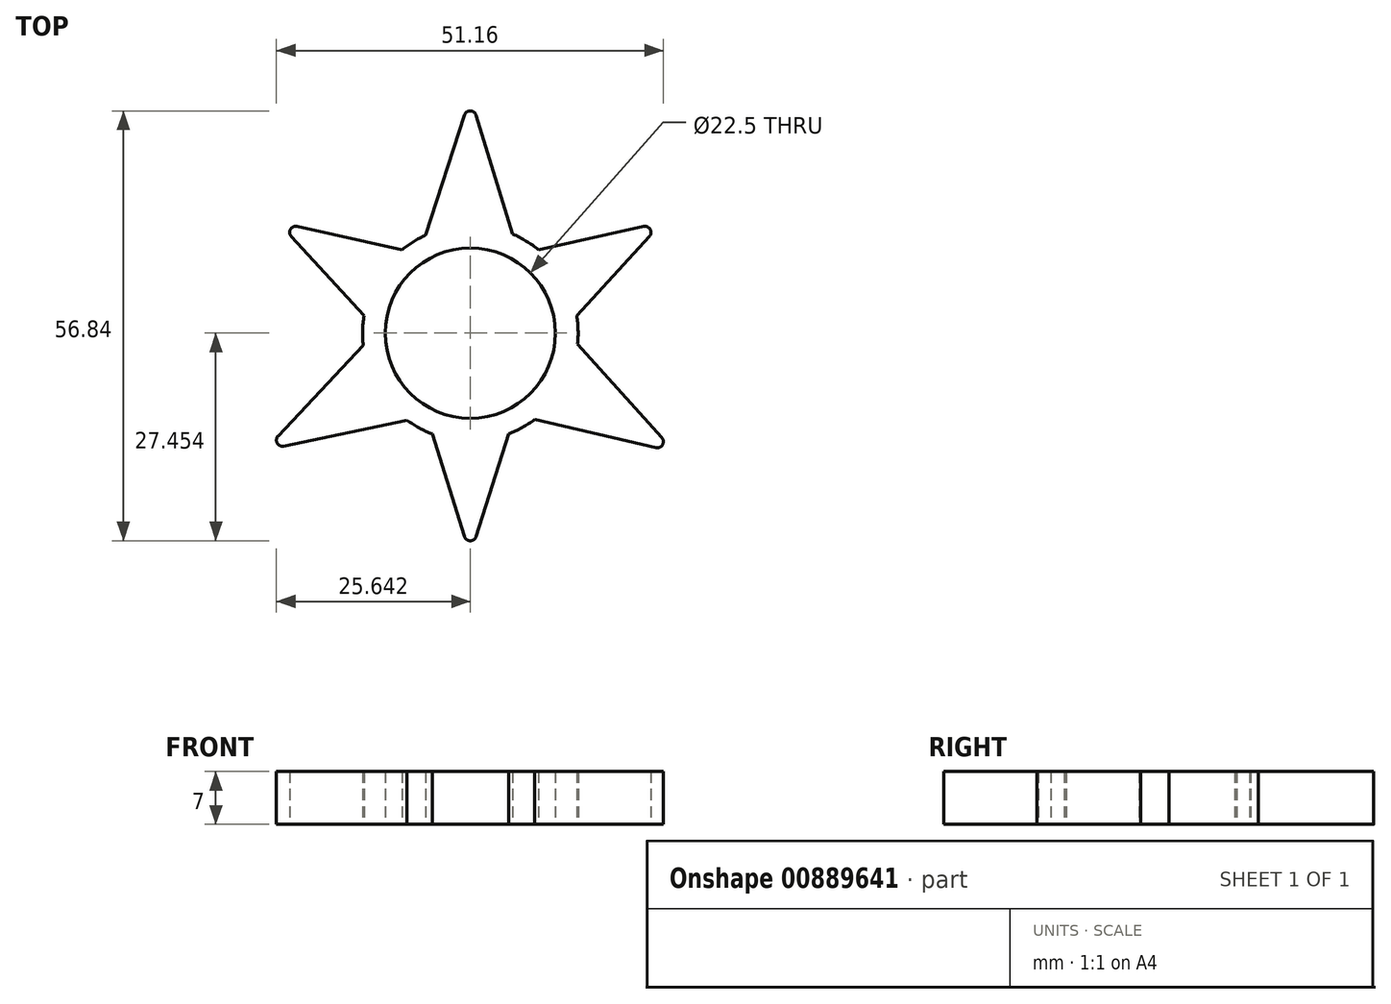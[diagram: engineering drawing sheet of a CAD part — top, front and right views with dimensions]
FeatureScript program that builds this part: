
annotation { "Feature Type Name" : "Feature", "Feature Type Description" : "" }
export const myFeature = defineFeature(function(context is Context, id is Id, definition is map)
    precondition{}
    {
        {
            var Q0;
            Q0=qCreatedBy(makeId("Top.planeOp"),FACE);
            var sketch = newSketch(context, id + "F0", { "sketchPlane" : qUnion([Q0])});
            skCircle(sketch, "E0", {"center": v(-0.33, -1.96) * mm, "radius": 11.25 * mm});
            skLineSegment(sketch, "E1", {"start": v(-7.64, 6.6) * mm, "end": v(-0.33, 29.3) * mm});
            skLineSegment(sketch, "E2", {"start": v(-0.33, 29.3) * mm, "end": v(6.57, 6.93) * mm});
            skLineSegment(sketch, "E3.1.0", {"start": v(26.68, -17.67) * mm, "end": v(3.88, -12.39) * mm});
            skLineSegment(sketch, "E3.1.1", {"start": v(10.74, 0.06) * mm, "end": v(26.68, -17.67) * mm});
            skLineSegment(sketch, "E3.2.0", {"start": v(-27.5, -17.4) * mm, "end": v(-11.46, -0.35) * mm});
            skLineSegment(sketch, "E3.2.1", {"start": v(-4.15, -12.54) * mm, "end": v(-27.5, -17.4) * mm});
            skLineSegment(sketch, "E4", {"start": v(-6.63, -11.27) * mm, "end": v(-0.33, -31.27) * mm});
            skLineSegment(sketch, "E5", {"start": v(-0.33, -31.27) * mm, "end": v(5.98, -11.27) * mm});
            skLineSegment(sketch, "E6.1.0", {"start": v(25.06, 12.7) * mm, "end": v(4.59, 8.16) * mm});
            skLineSegment(sketch, "E6.1.1", {"start": v(10.9, -2.76) * mm, "end": v(25.06, 12.7) * mm});
            skLineSegment(sketch, "E6.2.0", {"start": v(-25.72, 12.7) * mm, "end": v(-11.55, -2.76) * mm});
            skLineSegment(sketch, "E6.2.1", {"start": v(-5.24, 8.16) * mm, "end": v(-25.72, 12.7) * mm});
            skCircle(sketch, "E7", {"center": v(-0.33, -1.96) * mm, "radius": 14.25 * mm});
            skSolve(sketch);
        }
        {
            var Q0;
            {var subQ1=sQuery(id+"F0.wireOp",EDGE,"E0");var subQ5=sQuery(id+"F0.wireOp",EDGE,"E1");var subQ6=makeQuery(id+"F0.imprint","INTERSECT",VERTEX,{"derivedFrom":[subQ1,subQ5]});Q0=makeQuery(id+"F0.imprint","IMPRINT",FACE,{"disambiguationData":[TD([[makeQuery(id+"F0.imprint","IMPRINT",EDGE,{"disambiguationData":[TD([[subQ6,-1.0]])],"derivedFrom":subQ1}),-1.0]])]});}
            var Q1;
            {var subQ0=sQuery(id+"F0.wireOp",EDGE,"E7");var subQ1=sQuery(id+"F0.wireOp",EDGE,"E1");var subQ2=makeQuery(id+"F0.imprint","INTERSECT",VERTEX,{"derivedFrom":[subQ1,subQ0]});Q1=makeQuery(id+"F0.imprint","IMPRINT",FACE,{"disambiguationData":[TD([[makeQuery(id+"F0.imprint","IMPRINT",EDGE,{"disambiguationData":[TD([[subQ2,1.0]])],"derivedFrom":subQ1}),1.0]])]});}
            var Q2;
            {var subQ1=sQuery(id+"F0.wireOp",EDGE,"E0");var subQ5=sQuery(id+"F0.wireOp",EDGE,"E2");var subQ6=makeQuery(id+"F0.imprint","INTERSECT",VERTEX,{"derivedFrom":[subQ1,subQ5]});Q2=makeQuery(id+"F0.imprint","IMPRINT",FACE,{"disambiguationData":[TD([[makeQuery(id+"F0.imprint","IMPRINT",EDGE,{"disambiguationData":[TD([[subQ6,-1.0]])],"derivedFrom":subQ1}),-1.0]])]});}
            var Q3;
            {var subQ0=sQuery(id+"F0.wireOp",EDGE,"E2");var subQ1=sQuery(id+"F0.wireOp",EDGE,"E0");var subQ2=makeQuery(id+"F0.imprint","INTERSECT",VERTEX,{"derivedFrom":[subQ1,subQ0]});Q3=makeQuery(id+"F0.imprint","IMPRINT",FACE,{"disambiguationData":[TD([[makeQuery(id+"F0.imprint","IMPRINT",EDGE,{"disambiguationData":[TD([[subQ2,1.0]])],"derivedFrom":subQ1}),-1.0]])]});}
            var Q4;
            {var subQ3=sQuery(id+"F0.wireOp",EDGE,"E3.1.1");var subQ6=sQuery(id+"F0.wireOp",EDGE,"E0");var subQ9=makeQuery(id+"F0.imprint","INTERSECT",VERTEX,{"derivedFrom":[subQ6,subQ3]});Q4=makeQuery(id+"F0.imprint","IMPRINT",FACE,{"disambiguationData":[TD([[makeQuery(id+"F0.imprint","IMPRINT",EDGE,{"disambiguationData":[TD([[subQ9,-1.0]])],"derivedFrom":subQ6}),-1.0]])]});}
            var Q5;
            {var subQ1=sQuery(id+"F0.wireOp",EDGE,"E0");var subQ7=sQuery(id+"F0.wireOp",EDGE,"E3.1.0");var subQ8=makeQuery(id+"F0.imprint","INTERSECT",VERTEX,{"derivedFrom":[subQ1,subQ7]});Q5=makeQuery(id+"F0.imprint","IMPRINT",FACE,{"disambiguationData":[TD([[makeQuery(id+"F0.imprint","IMPRINT",EDGE,{"disambiguationData":[TD([[subQ8,-1.0]])],"derivedFrom":subQ1}),-1.0]])]});}
            var Q6;
            {var subQ0=sQuery(id+"F0.wireOp",EDGE,"E3.1.0");var subQ1=sQuery(id+"F0.wireOp",EDGE,"E0");var subQ2=makeQuery(id+"F0.imprint","INTERSECT",VERTEX,{"derivedFrom":[subQ1,subQ0]});Q6=makeQuery(id+"F0.imprint","IMPRINT",FACE,{"disambiguationData":[TD([[makeQuery(id+"F0.imprint","IMPRINT",EDGE,{"disambiguationData":[TD([[subQ2,1.0]])],"derivedFrom":subQ1}),-1.0]])]});}
            var Q7;
            {var subQ1=sQuery(id+"F0.wireOp",EDGE,"E0");var subQ5=sQuery(id+"F0.wireOp",EDGE,"E3.2.1");var subQ6=makeQuery(id+"F0.imprint","INTERSECT",VERTEX,{"derivedFrom":[subQ1,subQ5]});Q7=makeQuery(id+"F0.imprint","IMPRINT",FACE,{"disambiguationData":[TD([[makeQuery(id+"F0.imprint","IMPRINT",EDGE,{"disambiguationData":[TD([[subQ6,-1.0]])],"derivedFrom":subQ1}),-1.0]])]});}
            var Q8;
            {var subQ5=sQuery(id+"F0.wireOp",EDGE,"E3.2.0");var subQ6=sQuery(id+"F0.wireOp",EDGE,"E0");var subQ7=makeQuery(id+"F0.imprint","INTERSECT",VERTEX,{"derivedFrom":[subQ6,subQ5]});Q8=makeQuery(id+"F0.imprint","IMPRINT",FACE,{"disambiguationData":[TD([[makeQuery(id+"F0.imprint","IMPRINT",EDGE,{"disambiguationData":[TD([[subQ7,-1.0]])],"derivedFrom":subQ6}),-1.0]])]});}
            var Q9;
            {var subQ0=sQuery(id+"F0.wireOp",EDGE,"E6.2.1");var subQ1=sQuery(id+"F0.wireOp",EDGE,"E6.2.0");var subQ2=makeQuery(id+"F0.imprint","INTERSECT",VERTEX,{"derivedFrom":[subQ1,subQ0]});Q9=makeQuery(id+"F0.imprint","IMPRINT",FACE,{"disambiguationData":[TD([[makeQuery(id+"F0.imprint","IMPRINT",EDGE,{"disambiguationData":[TD([[subQ2,-1.0]])],"derivedFrom":subQ1}),1.0]])]});}
            var Q10;
            {var subQ0=sQuery(id+"F0.wireOp",EDGE,"E2");var subQ1=sQuery(id+"F0.wireOp",EDGE,"E1");var subQ2=makeQuery(id+"F0.imprint","INTERSECT",VERTEX,{"derivedFrom":[subQ1,subQ0]});Q10=makeQuery(id+"F0.imprint","IMPRINT",FACE,{"disambiguationData":[TD([[makeQuery(id+"F0.imprint","IMPRINT",EDGE,{"disambiguationData":[TD([[subQ2,1.0]])],"derivedFrom":subQ1}),-1.0]])]});}
            var Q11;
            {var subQ0=sQuery(id+"F0.wireOp",EDGE,"E6.1.1");var subQ1=sQuery(id+"F0.wireOp",EDGE,"E6.1.0");var subQ2=makeQuery(id+"F0.imprint","INTERSECT",VERTEX,{"derivedFrom":[subQ1,subQ0]});Q11=makeQuery(id+"F0.imprint","IMPRINT",FACE,{"disambiguationData":[TD([[makeQuery(id+"F0.imprint","IMPRINT",EDGE,{"disambiguationData":[TD([[subQ2,-1.0]])],"derivedFrom":subQ1}),1.0]])]});}
            var Q12;
            {var subQ0=sQuery(id+"F0.wireOp",EDGE,"E3.1.1");var subQ1=sQuery(id+"F0.wireOp",EDGE,"E3.1.0");var subQ2=makeQuery(id+"F0.imprint","INTERSECT",VERTEX,{"derivedFrom":[subQ1,subQ0]});Q12=makeQuery(id+"F0.imprint","IMPRINT",FACE,{"disambiguationData":[TD([[makeQuery(id+"F0.imprint","IMPRINT",EDGE,{"disambiguationData":[TD([[subQ2,-1.0]])],"derivedFrom":subQ1}),-1.0]])]});}
            var Q13;
            {var subQ0=sQuery(id+"F0.wireOp",EDGE,"E5");var subQ1=sQuery(id+"F0.wireOp",EDGE,"E4");var subQ2=makeQuery(id+"F0.imprint","INTERSECT",VERTEX,{"derivedFrom":[subQ1,subQ0]});Q13=makeQuery(id+"F0.imprint","IMPRINT",FACE,{"disambiguationData":[TD([[makeQuery(id+"F0.imprint","IMPRINT",EDGE,{"disambiguationData":[TD([[subQ2,1.0]])],"derivedFrom":subQ1}),1.0]])]});}
            var Q14;
            {var subQ0=sQuery(id+"F0.wireOp",EDGE,"E3.2.1");var subQ1=sQuery(id+"F0.wireOp",EDGE,"E3.2.0");var subQ2=makeQuery(id+"F0.imprint","INTERSECT",VERTEX,{"derivedFrom":[subQ1,subQ0]});Q14=makeQuery(id+"F0.imprint","IMPRINT",FACE,{"disambiguationData":[TD([[makeQuery(id+"F0.imprint","IMPRINT",EDGE,{"disambiguationData":[TD([[subQ2,-1.0]])],"derivedFrom":subQ1}),-1.0]])]});}
            var Q15;
            {var subQ0=sQuery(id+"F0.wireOp",EDGE,"E3.2.0");var subQ1=sQuery(id+"F0.wireOp",EDGE,"E0");var subQ2=makeQuery(id+"F0.imprint","INTERSECT",VERTEX,{"derivedFrom":[subQ1,subQ0]});Q15=makeQuery(id+"F0.imprint","IMPRINT",FACE,{"disambiguationData":[TD([[makeQuery(id+"F0.imprint","IMPRINT",EDGE,{"disambiguationData":[TD([[subQ2,1.0]])],"derivedFrom":subQ1}),-1.0]])]});}
            var Q16;
            {var subQ0=sQuery(id+"F0.wireOp",EDGE,"E7");var subQ1=sQuery(id+"F0.wireOp",EDGE,"E3.2.1");var subQ2=makeQuery(id+"F0.imprint","INTERSECT",VERTEX,{"derivedFrom":[subQ1,subQ0]});Q16=makeQuery(id+"F0.imprint","IMPRINT",FACE,{"disambiguationData":[TD([[makeQuery(id+"F0.imprint","IMPRINT",EDGE,{"disambiguationData":[TD([[subQ2,1.0]])],"derivedFrom":subQ1}),1.0]])]});}
            var Q17;
            {var subQ0=sQuery(id+"F0.wireOp",EDGE,"E7");var subQ1=sQuery(id+"F0.wireOp",EDGE,"E3.1.1");var subQ2=makeQuery(id+"F0.imprint","INTERSECT",VERTEX,{"derivedFrom":[subQ1,subQ0]});Q17=makeQuery(id+"F0.imprint","IMPRINT",FACE,{"disambiguationData":[TD([[makeQuery(id+"F0.imprint","IMPRINT",EDGE,{"disambiguationData":[TD([[subQ2,1.0]])],"derivedFrom":subQ1}),1.0]])]});}
            var Q18;
            {var subQ0=sQuery(id+"F0.wireOp",EDGE,"E7");var subQ1=sQuery(id+"F0.wireOp",EDGE,"E3.2.0");var subQ2=makeQuery(id+"F0.imprint","INTERSECT",VERTEX,{"derivedFrom":[subQ1,subQ0]});Q18=makeQuery(id+"F0.imprint","IMPRINT",FACE,{"disambiguationData":[TD([[makeQuery(id+"F0.imprint","IMPRINT",EDGE,{"disambiguationData":[TD([[subQ2,-1.0]])],"derivedFrom":subQ1}),1.0]])]});}
            var Q19;
            {var subQ3=sQuery(id+"F0.wireOp",EDGE,"E4");var subQ5=sQuery(id+"F0.wireOp",EDGE,"E0");var subQ6=makeQuery(id+"F0.imprint","INTERSECT",VERTEX,{"derivedFrom":[subQ5,subQ3]});Q19=makeQuery(id+"F0.imprint","IMPRINT",FACE,{"disambiguationData":[TD([[makeQuery(id+"F0.imprint","IMPRINT",EDGE,{"disambiguationData":[TD([[subQ6,1.0]])],"derivedFrom":subQ5}),-1.0]])]});}
            var Q20;
            {var subQ0=sQuery(id+"F0.wireOp",EDGE,"E3.2.1");var subQ1=sQuery(id+"F0.wireOp",EDGE,"E0");var subQ2=makeQuery(id+"F0.imprint","INTERSECT",VERTEX,{"derivedFrom":[subQ1,subQ0]});Q20=makeQuery(id+"F0.imprint","IMPRINT",FACE,{"disambiguationData":[TD([[makeQuery(id+"F0.imprint","IMPRINT",EDGE,{"disambiguationData":[TD([[subQ2,1.0]])],"derivedFrom":subQ1}),-1.0]])]});}
            var Q21;
            {var subQ0=sQuery(id+"F0.wireOp",EDGE,"E7");var subQ1=sQuery(id+"F0.wireOp",EDGE,"E3.1.0");var subQ2=makeQuery(id+"F0.imprint","INTERSECT",VERTEX,{"derivedFrom":[subQ1,subQ0]});Q21=makeQuery(id+"F0.imprint","IMPRINT",FACE,{"disambiguationData":[TD([[makeQuery(id+"F0.imprint","IMPRINT",EDGE,{"disambiguationData":[TD([[subQ2,-1.0]])],"derivedFrom":subQ1}),1.0]])]});}
            var Q22;
            {var subQ7=sQuery(id+"F0.wireOp",EDGE,"E5");var subQ9=sQuery(id+"F0.wireOp",EDGE,"E0");var subQ10=makeQuery(id+"F0.imprint","INTERSECT",VERTEX,{"derivedFrom":[subQ9,subQ7]});Q22=makeQuery(id+"F0.imprint","IMPRINT",FACE,{"disambiguationData":[TD([[makeQuery(id+"F0.imprint","IMPRINT",EDGE,{"disambiguationData":[TD([[subQ10,-1.0]])],"derivedFrom":subQ9}),-1.0]])]});}
            var Q23;
            {var subQ0=sQuery(id+"F0.wireOp",EDGE,"E3.1.1");var subQ1=sQuery(id+"F0.wireOp",EDGE,"E0");var subQ2=makeQuery(id+"F0.imprint","INTERSECT",VERTEX,{"derivedFrom":[subQ1,subQ0]});Q23=makeQuery(id+"F0.imprint","IMPRINT",FACE,{"disambiguationData":[TD([[makeQuery(id+"F0.imprint","IMPRINT",EDGE,{"disambiguationData":[TD([[subQ2,1.0]])],"derivedFrom":subQ1}),-1.0]])]});}
            var Q24;
            {var subQ3=sQuery(id+"F0.wireOp",EDGE,"E6.1.0");var subQ5=sQuery(id+"F0.wireOp",EDGE,"E0");var subQ6=makeQuery(id+"F0.imprint","INTERSECT",VERTEX,{"derivedFrom":[subQ5,subQ3]});Q24=makeQuery(id+"F0.imprint","IMPRINT",FACE,{"disambiguationData":[TD([[makeQuery(id+"F0.imprint","IMPRINT",EDGE,{"disambiguationData":[TD([[subQ6,-1.0]])],"derivedFrom":subQ5}),-1.0]])]});}
            var Q25;
            {var subQ0=sQuery(id+"F0.wireOp",EDGE,"E7");var subQ1=sQuery(id+"F0.wireOp",EDGE,"E2");var subQ2=makeQuery(id+"F0.imprint","INTERSECT",VERTEX,{"derivedFrom":[subQ1,subQ0]});Q25=makeQuery(id+"F0.imprint","IMPRINT",FACE,{"disambiguationData":[TD([[makeQuery(id+"F0.imprint","IMPRINT",EDGE,{"disambiguationData":[TD([[subQ2,-1.0]])],"derivedFrom":subQ1}),1.0]])]});}
            var Q26;
            {var subQ0=sQuery(id+"F0.wireOp",EDGE,"E1");var subQ1=sQuery(id+"F0.wireOp",EDGE,"E0");var subQ2=makeQuery(id+"F0.imprint","INTERSECT",VERTEX,{"derivedFrom":[subQ1,subQ0]});Q26=makeQuery(id+"F0.imprint","IMPRINT",FACE,{"disambiguationData":[TD([[makeQuery(id+"F0.imprint","IMPRINT",EDGE,{"disambiguationData":[TD([[subQ2,1.0]])],"derivedFrom":subQ1}),-1.0]])]});}
            extrude(context, id + "F1", {"entities" : qUnion([Q0, Q1, Q2, Q3, Q4, Q5, Q6, Q7, Q8, Q9, Q10, Q11, Q12, Q13, Q14, Q15, Q16, Q17, Q18, Q19, Q20, Q21, Q22, Q23, Q24, Q25, Q26]), "depth" : 7 * mm, "offsetDistance" : 25 * mm});
        }
        {
            var Q0;
            Q0=makeQuery(id+"F1.opExtrude","SWEPT_EDGE",EDGE,{"disambiguationData":[OSD([sQuery(id+"F0.wireOp",EDGE,"E4"),sQuery(id+"F0.wireOp",EDGE,"E5")])]});
            var Q1;
            Q1=makeQuery(id+"F1.opExtrude","SWEPT_EDGE",EDGE,{"disambiguationData":[OSD([sQuery(id+"F0.wireOp",EDGE,"E3.1.0"),sQuery(id+"F0.wireOp",EDGE,"E3.1.1")])]});
            var Q2;
            Q2=makeQuery(id+"F1.opExtrude","SWEPT_EDGE",EDGE,{"disambiguationData":[OSD([sQuery(id+"F0.wireOp",EDGE,"E6.1.0"),sQuery(id+"F0.wireOp",EDGE,"E6.1.1")])]});
            var Q3;
            Q3=makeQuery(id+"F1.opExtrude","SWEPT_EDGE",EDGE,{"disambiguationData":[OSD([sQuery(id+"F0.wireOp",EDGE,"E3.2.0"),sQuery(id+"F0.wireOp",EDGE,"E3.2.1")])]});
            var Q4;
            Q4=makeQuery(id+"F1.opExtrude","SWEPT_EDGE",EDGE,{"disambiguationData":[OSD([sQuery(id+"F0.wireOp",EDGE,"E6.2.0"),sQuery(id+"F0.wireOp",EDGE,"E6.2.1")])]});
            var Q5;
            Q5=makeQuery(id+"F1.opExtrude","SWEPT_EDGE",EDGE,{"disambiguationData":[OSD([sQuery(id+"F0.wireOp",EDGE,"E1"),sQuery(id+"F0.wireOp",EDGE,"E2")])]});
            fillet(context, id + "F2", {"entities" : qUnion([Q0, Q1, Q2, Q3, Q4, Q5]), "radius" : 0.8 * mm, "tangentPropagation" : true, "allowEdgeOverflow" : false});
        }
    });
